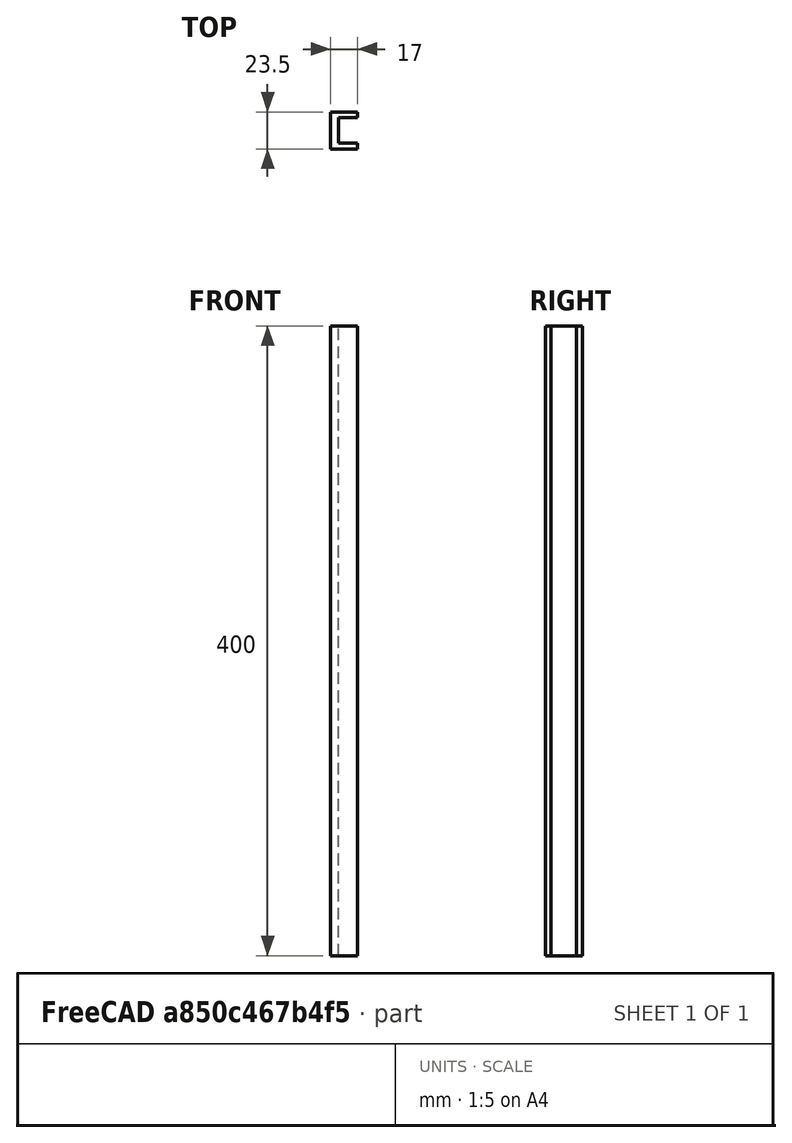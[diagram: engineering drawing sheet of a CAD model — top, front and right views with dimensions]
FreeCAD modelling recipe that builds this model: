
FCSTD DOCUMENT  (FreeCAD 2023.1231R38924 (Git))
Label: SteelBeam
License: All rights reserved
LicenseURL: https://en.wikipedia.org/wiki/All_rights_reserved
objects: Sketcher::SketchObject×1, PartDesign::Pad×1, PartDesign::Body×1, App::Part×1
note: 6 computed .brp shape members not serialized (recipe doc carries the construction recipe); baked Part::Feature solids carry a one-line shape summary decoded from their .brp

FEATURE [Sketcher::SketchObject] Sketch
  ArcFitTolerance = 1e-06
  AttachmentSupport = -> [XY_Plane]
  ExternalBSplineMaxDegree = 5
  ExternalBSplineTolerance = 0.0001
  FullyConstrained = true
  InternalTolerance = 1e-06
  InvalidShape = false
  MakeInternals = false
  MapMode = 5
  Support = -> [XY_Plane]
  TreeRank = 13
  ValidateShape = false
  sketch-geometry (8):
    g0: LineSegment StartX=0 StartY=11.75 StartZ=0 EndX=0 EndY=-11.75 EndZ=0
    g1: LineSegment StartX=0 StartY=-11.75 StartZ=0 EndX=17 EndY=-11.75 EndZ=0
    g2: LineSegment StartX=17 StartY=-11.75 StartZ=0 EndX=17 EndY=-8 EndZ=0
    g3: LineSegment StartX=17 StartY=-8 StartZ=0 EndX=5 EndY=-8 EndZ=0
    g4: LineSegment StartX=5 StartY=-8 StartZ=0 EndX=5 EndY=8 EndZ=0
    g5: LineSegment StartX=5 StartY=8 StartZ=0 EndX=17 EndY=8 EndZ=0
    g6: LineSegment StartX=17 StartY=8 StartZ=0 EndX=17 EndY=11.75 EndZ=0
    g7: LineSegment StartX=17 StartY=11.75 StartZ=0 EndX=0 EndY=11.75 EndZ=0
  constraints (23):
    c: Coincident(g0,g1)
    c: Coincident(g1,g2)
    c: Vertical(g2)
    c: Coincident(g2,g3)
    c: Horizontal(g3)
    c: Coincident(g3,g4)
    c: Vertical(g4)
    c: Coincident(g4,g5)
    c: Horizontal(g5)
    c: Coincident(g5,g6)
    c: Coincident(g6,g7)
    c: Coincident(g7,g0)
    c: Symmetric(g0,g0,g-1)
    c: Vertical(g0)
    c: Horizontal(g7)
    c: Horizontal(g1)
    c: Vertical(g2,g5)
    c: Vertical(g5,g6)
    c: Equal(g2,g6)
    c: DistanceY(g0,g0) = 23.5
    c: DistanceY(g4,g4) = 16
    c: DistanceX(g7,g7) = 17
    c: DistanceX(g5,g5) = 12
FEATURE [PartDesign::Pad] Pad
  AddSubType = 0
  AlongSketchNormal = false
  AutoTaperInnerAngle = true
  CheckUpToFaceLimits = true
  ClaimChildren = false
  Direction = (0,0,1)
  Fit = 0
  FitJoin = 0
  InnerFit = 0
  InnerFitJoin = 0
  InvalidShape = false
  Length = 400
  Length2 = 10
  Linearize = true
  NewSolid = false
  Profile = -> Sketch
  ReferenceAxis = -> Sketch [N_Axis]
  Suppress = false
  TaperInnerAngle = 0
  TaperInnerAngleRev = 0
  TreeRank = 14
  Type = 0
  ValidateShape = true
  _ProfileBasedVersion = 1
FEATURE [PartDesign::Body] Body
  AutoGroupSolids = false
  ClaimAllChildren = false
  ExportMode = 0
  Group = -> [Sketch,Pad]
  InvalidShape = false
  Origin = -> Origin001
  Tip = -> Pad
  TreeRank = 12
  ValidateShape = false
  _ExportChildren = -> [Pad]
  _GroupVersion = 1
FEATURE [App::Part] Part  label="Beam"
  ClaimAllChildren = false
  ExportMode = 1
  Group = -> [Body]
  Origin = -> Origin
  TreeRank = 1
  _ExportChildren = -> [Body]
  _GroupVersion = 1
